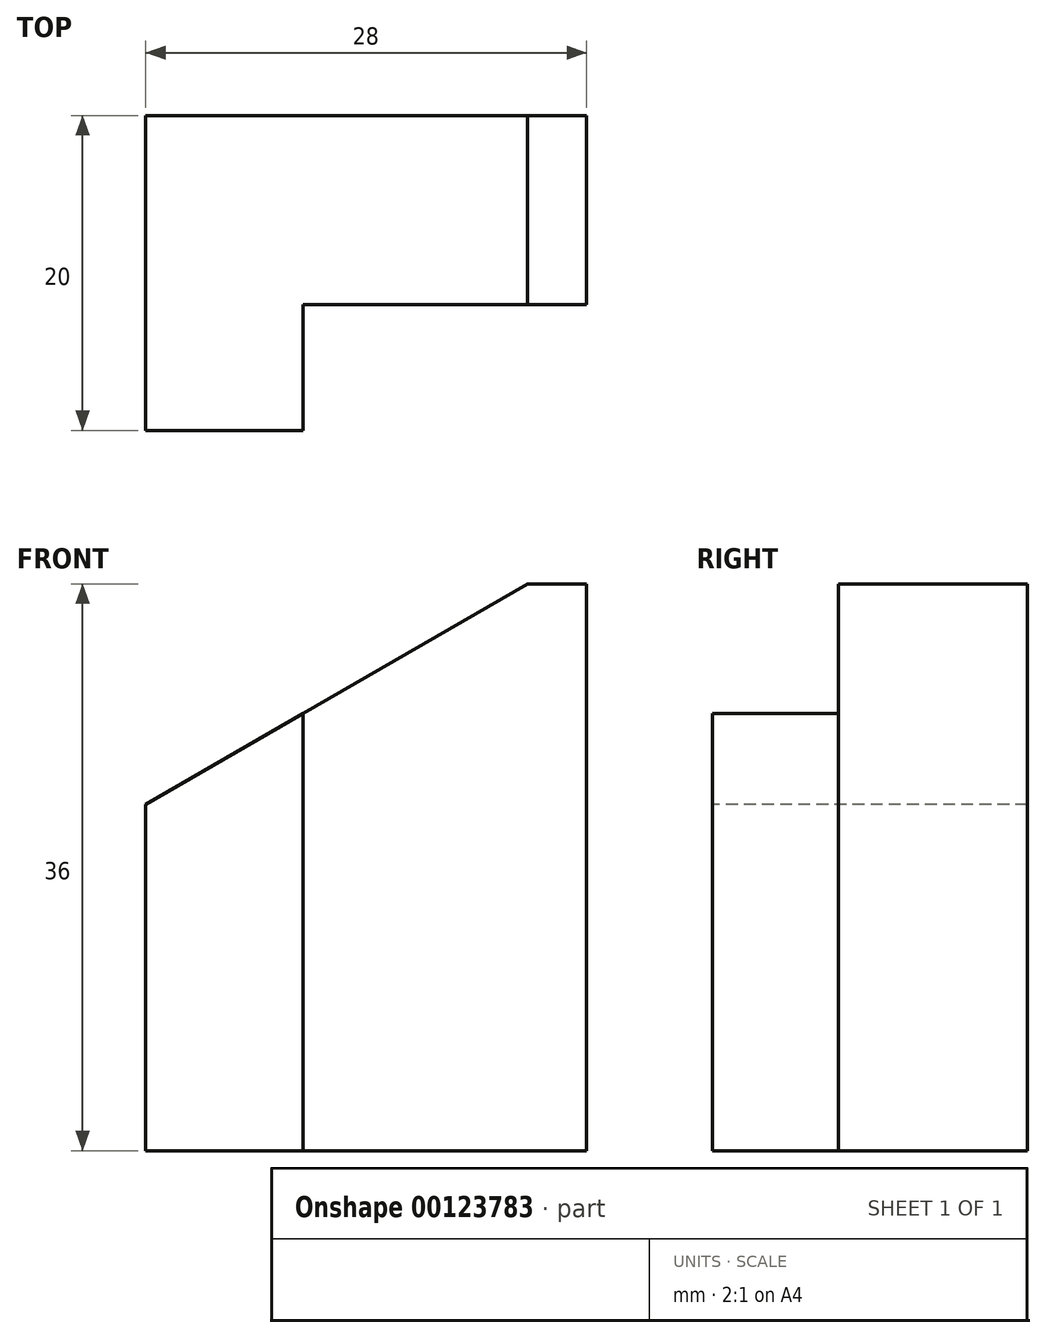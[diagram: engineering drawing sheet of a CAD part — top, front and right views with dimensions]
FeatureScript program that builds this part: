
annotation { "Feature Type Name" : "Feature", "Feature Type Description" : "" }
export const myFeature = defineFeature(function(context is Context, id is Id, definition is map)
    precondition{}
    {
        {
            var Q0;
            Q0=qCreatedBy(makeId("Top.planeOp"),FACE);
            var sketch = newSketch(context, id + "F0", { "sketchPlane" : qUnion([Q0])});
            skLineSegment(sketch, "E0", {"start": v(0, 0) * mm, "end": v(0, 20) * mm});
            skLineSegment(sketch, "E1", {"start": v(0, 20) * mm, "end": v(28, 20) * mm});
            skLineSegment(sketch, "E2", {"start": v(28, 20) * mm, "end": v(28, 8) * mm});
            skLineSegment(sketch, "E3", {"start": v(28, 8) * mm, "end": v(10, 8) * mm});
            skLineSegment(sketch, "E4", {"start": v(10, 8) * mm, "end": v(10, 0) * mm});
            skLineSegment(sketch, "E5", {"start": v(10, 0) * mm, "end": v(0, 0) * mm});
            skSolve(sketch);
        }
        {
            var Q0;
            Q0=makeQuery(id+"F0.imprint","IMPRINT",FACE,{"disambiguationData":[TD([[makeQuery(id+"F0.imprint","IMPRINT",EDGE,{"derivedFrom":sQuery(id+"F0.wireOp",EDGE,"E0")}),-1.0]])]});
            extrude(context, id + "F1", {"entities" : qUnion([Q0]), "depth" : 36 * mm});
        }
        {
            var Q0;
            Q0=qCreatedBy(makeId("Front.planeOp"),FACE);
            var sketch = newSketch(context, id + "F2", { "sketchPlane" : qUnion([Q0])});
            skLineSegment(sketch, "E6", {"start": v(0, 36) * mm, "end": v(0, 22) * mm});
            skLineSegment(sketch, "E7", {"start": v(0, 22) * mm, "end": v(24.25, 36) * mm});
            skLineSegment(sketch, "E8", {"start": v(24.25, 36) * mm, "end": v(0, 36) * mm});
            skSolve(sketch);
        }
        {
            var Q0;
            Q0 = qSketchRegion(id + "F2", true);
            extrude(context, id + "F3", {"entities" : qUnion([Q0]), "operationType" : NewBodyOperationType.REMOVE, "endBound" : BoundingType.THROUGH_ALL, "oppositeDirection" : true, "depth" : 25 * mm});
        }
    });
